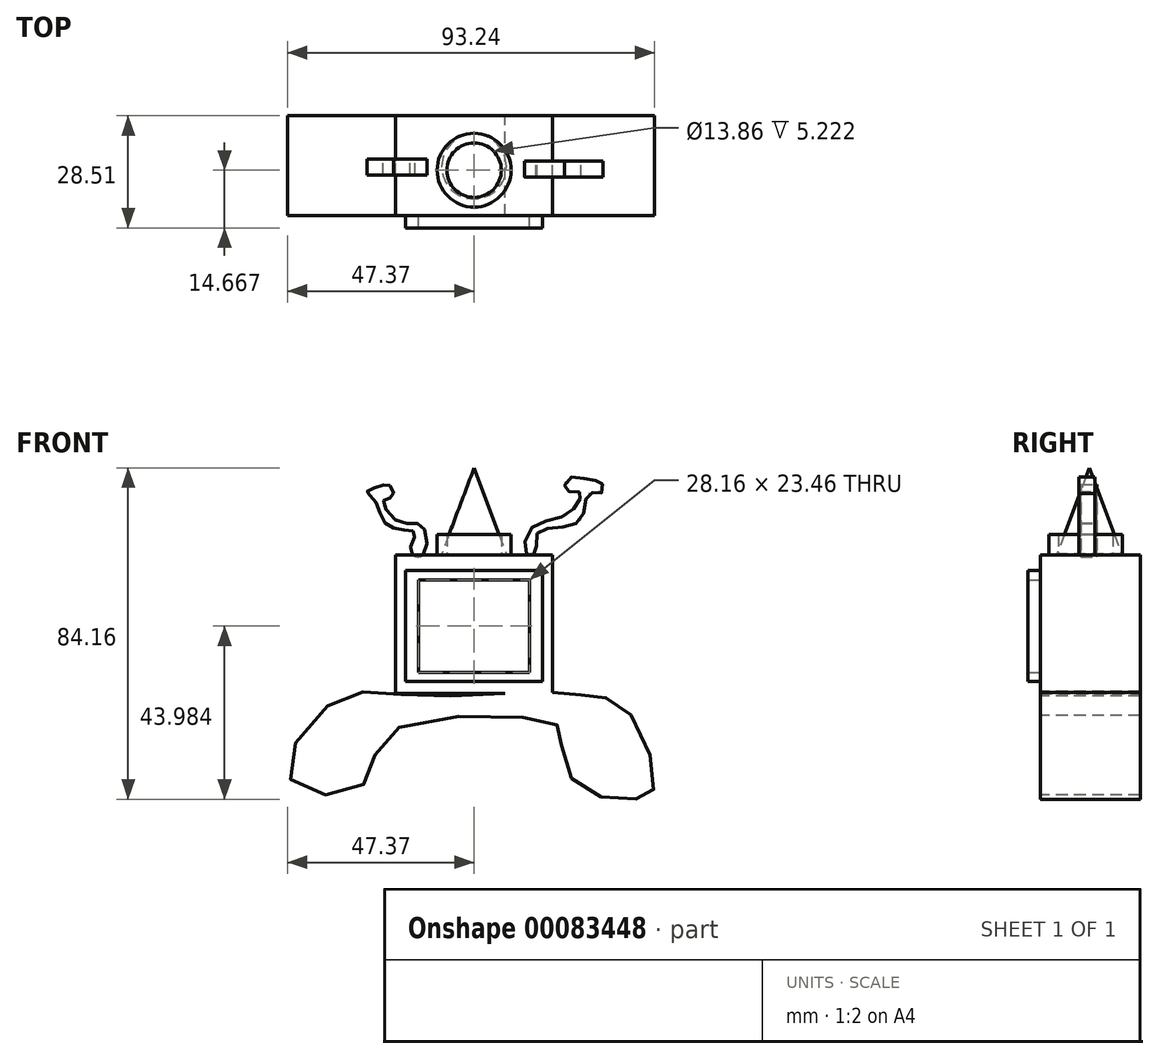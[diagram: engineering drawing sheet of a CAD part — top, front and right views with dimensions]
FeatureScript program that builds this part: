
annotation { "Feature Type Name" : "Feature", "Feature Type Description" : "" }
export const myFeature = defineFeature(function(context is Context, id is Id, definition is map)
    precondition{}
    {
        {
            var Q0;
            Q0=qCreatedBy(makeId("Front.planeOp"),FACE);
            var sketch = newSketch(context, id + "F0", { "sketchPlane" : qUnion([Q0])});
            skLineSegment(sketch, "E0.bottom", {"start": v(-19.94, 53.73) * mm, "end": v(19.94, 53.73) * mm});
            skLineSegment(sketch, "E0.top", {"start": v(-19.94, 18.54) * mm, "end": v(19.94, 18.54) * mm});
            skLineSegment(sketch, "E0.left", {"start": v(-19.94, 53.73) * mm, "end": v(-19.94, 18.54) * mm});
            skLineSegment(sketch, "E0.right", {"start": v(19.94, 53.73) * mm, "end": v(19.94, 18.54) * mm});
            skPoint(sketch, "E0.middle", {"position": v(0, 36.13) * mm});
            skSolve(sketch);
        }
        {
            var Q0;
            Q0 = qSketchRegion(id + "F0", true);
            extrude(context, id + "F1", {"entities" : qUnion([Q0]), "depth" : 25.4 * mm});
        }
        {
            var Q0;
            Q0=makeQuery(id+"F1.opExtrude","CAP_FACE",FACE,{"disambiguationData":[OSD([sQuery(id+"F0.wireOp",EDGE,"E0.bottom"),sQuery(id+"F0.wireOp",EDGE,"E0.top"),sQuery(id+"F0.wireOp",EDGE,"E0.left"),sQuery(id+"F0.wireOp",EDGE,"E0.right")])],"isStart":false});
            var sketch = newSketch(context, id + "F2", { "sketchPlane" : qUnion([Q0])});
            skLineSegment(sketch, "E1.bottom", {"start": v(-17.36, 49.74) * mm, "end": v(17.36, 49.74) * mm});
            skLineSegment(sketch, "E1.top", {"start": v(-17.36, 21.59) * mm, "end": v(17.36, 21.59) * mm});
            skLineSegment(sketch, "E1.left", {"start": v(-17.36, 49.74) * mm, "end": v(-17.36, 21.59) * mm});
            skLineSegment(sketch, "E1.right", {"start": v(17.36, 49.74) * mm, "end": v(17.36, 21.59) * mm});
            skPoint(sketch, "E1.middle", {"position": v(0, 35.66) * mm});
            skLineSegment(sketch, "E2.bottom", {"start": v(-14.08, 47.4) * mm, "end": v(14.08, 47.4) * mm});
            skLineSegment(sketch, "E2.top", {"start": v(-14.08, 23.93) * mm, "end": v(14.08, 23.93) * mm});
            skLineSegment(sketch, "E2.left", {"start": v(-14.08, 47.4) * mm, "end": v(-14.08, 23.93) * mm});
            skLineSegment(sketch, "E2.right", {"start": v(14.08, 47.4) * mm, "end": v(14.08, 23.93) * mm});
            skSolve(sketch);
        }
        {
            var Q0;
            Q0 = qSketchRegion(id + "F2", true);
            extrude(context, id + "F3", {"entities" : qUnion([Q0]), "depth" : 3.1 * mm});
        }
        {
            var Q0;
            Q0=makeQuery(id+"F1.opExtrude","SWEPT_FACE",FACE,{"disambiguationData":[OSD([sQuery(id+"F0.wireOp",EDGE,"E0.bottom")])]});
            var sketch = newSketch(context, id + "F4", { "sketchPlane" : qUnion([Q0])});
            skCircle(sketch, "E3", {"center": v(0, -13.84) * mm, "radius": 9.4 * mm});
            skCircle(sketch, "E4", {"center": v(0, -13.84) * mm, "radius": 6.93 * mm});
            skSolve(sketch);
        }
        {
            var Q0;
            Q0 = qSketchRegion(id + "F4", true);
            extrude(context, id + "F5", {"entities" : qUnion([Q0]), "depth" : 5.22 * mm});
        }
        {
            var Q0;
            Q0=qCreatedBy(makeId("Front.planeOp"),FACE);
            var sketch = newSketch(context, id + "F6", { "sketchPlane" : qUnion([Q0])});
            skLineSegment(sketch, "E5", {"start": v(0, 54.02) * mm, "end": v(0, 75.84) * mm});
            skLineSegment(sketch, "E6", {"start": v(0, 75.84) * mm, "end": v(0, 54.02) * mm});
            skLineSegment(sketch, "E7", {"start": v(0, 54.02) * mm, "end": v(8.21, 54.02) * mm});
            skLineSegment(sketch, "E8", {"start": v(8.21, 54.02) * mm, "end": v(0, 75.84) * mm});
            skSolve(sketch);
        }
        {
            var Q0;
            Q0=makeQuery(id+"F6.imprint","IMPRINT",FACE,{"disambiguationData":[TD([[makeQuery(id+"F6.imprint","IMPRINT",EDGE,{"derivedFrom":sQuery(id+"F6.wireOp",EDGE,"E5")}),-1.0]])]});
            var Q1;
            Q1=sQuery(id+"F6.wireOp",EDGE,"E5");
            revolve(context, id + "F7", {"entities" : qUnion([Q0]), "axis" : qUnion([Q1]), "revolveType" : RevolveType.FULL});
        }
        {
            var Q0;
            Q0=makeQuery(id+"F7.opRevolve","SWEPT_BODY",BODY,{"disambiguationData":[OSD([sQuery(id+"F6.wireOp",EDGE,"E5"),sQuery(id+"F6.wireOp",EDGE,"E7"),sQuery(id+"F6.wireOp",EDGE,"E8")])]});
            transform(context, id + "F8", {"entities" : qUnion([Q0]), "transformType" : TransformType.TRANSLATION_3D, "dx" : 0 * mm, "dy" : -12.9 * mm, "dz" : 0 * mm, "makeCopy" : false});
        }
        {
            var Q0;
            Q0=qCreatedBy(makeId("Front.planeOp"),FACE);
            var sketch = newSketch(context, id + "F9", { "sketchPlane" : qUnion([Q0])});
            skFitSpline(sketch, "E9", {"points": [v(-12.9, 53.79) * mm, v(-13.37, 61.3) * mm, v(-18.77, 62) * mm, v(-23, 67.63) * mm, v(-20.65, 68.57) * mm, v(-21.35, 71.39) * mm, v(-24.17, 71.15) * mm, v(-27.22, 69.74) * mm, v(-25.34, 67.87) * mm, v(-22.76, 62) * mm, v(-17.6, 60.12) * mm, v(-15.02, 59.19) * mm, v(-16.19, 54.5) * mm, v(-12.9, 53.79) * mm]});
            skSolve(sketch);
        }
        {
            var Q0;
            Q0 = qSketchRegion(id + "F9", true);
            extrude(context, id + "F10", {"entities" : qUnion([Q0]), "depth" : 4.06 * mm});
        }
        {
            var Q0;
            Q0=makeQuery(id+"F10.opExtrude","SWEPT_BODY",BODY,{"disambiguationData":[OSD([sQuery(id+"F9.wireOp",EDGE,"E9")])]});
            transform(context, id + "F11", {"entities" : qUnion([Q0]), "transformType" : TransformType.TRANSLATION_3D, "dx" : 0 * mm, "dy" : -11.03 * mm, "dz" : 0 * mm, "makeCopy" : false});
        }
        {
            var Q0;
            Q0=qCreatedBy(makeId("Front.planeOp"),FACE);
            var sketch = newSketch(context, id + "F12", { "sketchPlane" : qUnion([Q0])});
            skFitSpline(sketch, "E10", {"points": [v(13.37, 54.02) * mm, v(14.55, 60.6) * mm, v(23, 63.64) * mm, v(26.98, 68.1) * mm, v(26.75, 69.74) * mm, v(23.23, 70.21) * mm, v(24.17, 73.26) * mm, v(29.56, 72.8) * mm, v(32.38, 72.1) * mm, v(32.38, 69.5) * mm, v(29.33, 69.5) * mm, v(27.45, 63.4) * mm, v(22.52, 60.83) * mm, v(15.96, 59.19) * mm, v(15.72, 54.26) * mm, v(13.37, 54.02) * mm]});
            skSolve(sketch);
        }
        {
            var Q0;
            Q0 = qSketchRegion(id + "F12", true);
            extrude(context, id + "F13", {"entities" : qUnion([Q0]), "depth" : 4.06 * mm});
        }
        {
            var Q0;
            Q0=makeQuery(id+"F13.opExtrude","SWEPT_BODY",BODY,{"disambiguationData":[OSD([sQuery(id+"F12.wireOp",EDGE,"E10")])]});
            transform(context, id + "F14", {"entities" : qUnion([Q0]), "transformType" : TransformType.TRANSLATION_3D, "dx" : 0 * mm, "dy" : -11.5 * mm, "dz" : 0 * mm, "makeCopy" : false});
        }
        {
            var Q0;
            Q0=qCreatedBy(makeId("Front.planeOp"),FACE);
            var sketch = newSketch(context, id + "F15", { "sketchPlane" : qUnion([Q0])});
            skFitSpline(sketch, "E11", {"points": [v(-15.96, 18.12) * mm, v(-35.2, 16.72) * mm, v(-46.7, -3.23) * mm, v(-28.4, -4.87) * mm, v(-22.06, 8.27) * mm, v(19.47, 11.32) * mm, v(21.82, 8.5) * mm, v(26.04, -4.63) * mm, v(41.53, -8.15) * mm, v(45.75, -5.34) * mm, v(38.71, 14.6) * mm, v(29.33, 17.89) * mm, v(18.54, 18.83) * mm, v(-15.96, 18.12) * mm]});
            skSolve(sketch);
        }
        {
            var Q0;
            Q0 = qSketchRegion(id + "F15", true);
            extrude(context, id + "F16", {"entities" : qUnion([Q0]), "operationType" : NewBodyOperationType.ADD, "depth" : 25.4 * mm});
        }
    });
